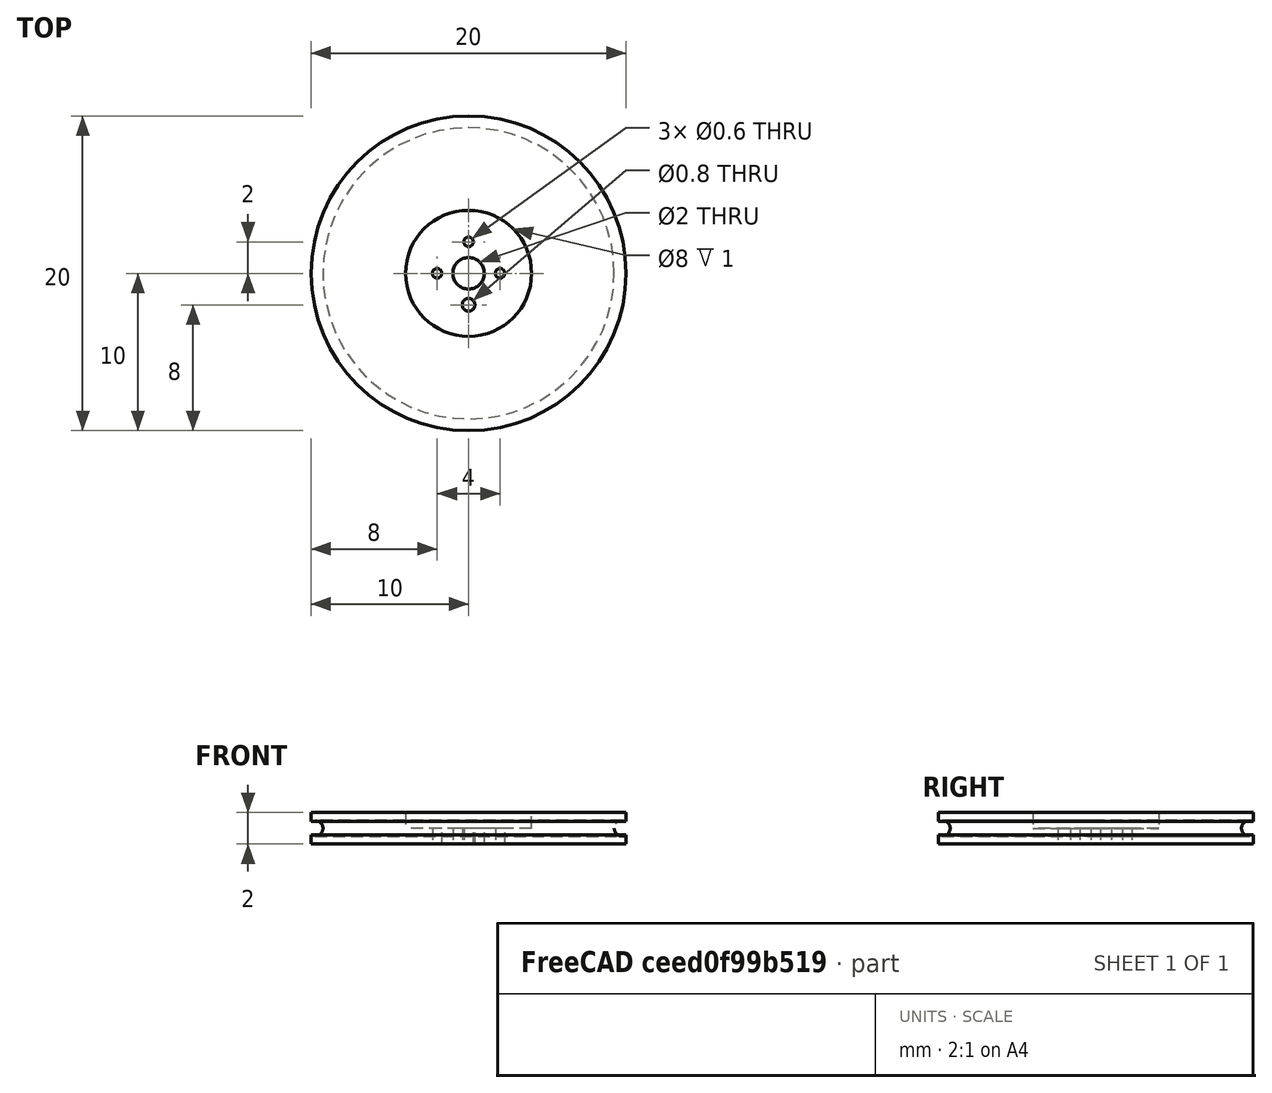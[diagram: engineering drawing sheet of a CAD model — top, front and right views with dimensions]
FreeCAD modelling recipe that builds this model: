
FCSTD DOCUMENT  (FreeCAD 0.20R29410 (Git))
Label: rueda
License: Creative Commons Attribution
LicenseURL: http://creativecommons.org/licenses/by/4.0/
objects: Part::Cylinder×7, Part::Cut×7, Part::Torus×1
note: 15 computed .brp shape members not serialized (recipe doc carries the construction recipe); baked Part::Feature solids carry a one-line shape summary decoded from their .brp

FEATURE [Part::Cylinder] Cylinder  label="Cilindro"
  Angle = 360
  AttacherType = Attacher::AttachEngine3D
  FirstAngle = 0
  Height = 2
  Radius = 10
  SecondAngle = 0
FEATURE [Part::Torus] Torus  label="Toro"
  Angle1 = -180
  Angle2 = 180
  Angle3 = 360
  AttacherType = Attacher::AttachEngine3D
  Placement = pos=(0,0,1) rot=(0,0,1;0rad)
  Radius1 = 9.75
  Radius2 = 0.5
FEATURE [Part::Cut] Cut
  Base = -> Cylinder
  Refine = true
  Tool = -> Torus
FEATURE [Part::Cylinder] Cylinder001  label="Cilindro001"
  Angle = 360
  AttacherType = Attacher::AttachEngine3D
  FirstAngle = 0
  Height = 1
  Placement = pos=(0,0,1) rot=(0,0,1;0rad)
  Radius = 4
  SecondAngle = 0
FEATURE [Part::Cut] Cut001  label="rueda con hueco"
  Base = -> Cut
  Refine = true
  Tool = -> Cylinder001
FEATURE [Part::Cylinder] Cylinder002  label="Cilindro002"
  Angle = 360
  AttacherType = Attacher::AttachEngine3D
  FirstAngle = 0
  Height = 10
  Radius = 1
  SecondAngle = 0
FEATURE [Part::Cut] Cut002
  Base = -> Cut001
  Refine = true
  Tool = -> Cylinder002
FEATURE [Part::Cylinder] Cylinder003  label="Cilindro003"
  Angle = 360
  AttacherType = Attacher::AttachEngine3D
  FirstAngle = 0
  Height = 10
  Placement = pos=(-2,0,0) rot=(0,0,1;0rad)
  Radius = 0.3
  SecondAngle = 0
FEATURE [Part::Cut] Cut003
  Base = -> Cut002
  Refine = true
  Tool = -> Cylinder003
FEATURE [Part::Cylinder] Cylinder004  label="Cilindro004"
  Angle = 360
  AttacherType = Attacher::AttachEngine3D
  FirstAngle = 0
  Height = 10
  Placement = pos=(2,0,0) rot=(0,0,1;0rad)
  Radius = 0.3
  SecondAngle = 0
FEATURE [Part::Cut] Cut004
  Base = -> Cut003
  Refine = true
  Tool = -> Cylinder004
FEATURE [Part::Cylinder] Cylinder005  label="Cilindro005"
  Angle = 360
  AttacherType = Attacher::AttachEngine3D
  FirstAngle = 0
  Height = 10
  Placement = pos=(0,2,0) rot=(0,0,1;0rad)
  Radius = 0.3
  SecondAngle = 0
FEATURE [Part::Cut] Cut005
  Base = -> Cut004
  Refine = true
  Tool = -> Cylinder005
FEATURE [Part::Cylinder] Cylinder006  label="Cilindro006"
  Angle = 360
  AttacherType = Attacher::AttachEngine3D
  FirstAngle = 0
  Height = 10
  Placement = pos=(0,-2,0) rot=(0,0,1;0rad)
  Radius = 0.4
  SecondAngle = 0
FEATURE [Part::Cut] Cut006  label="Rueda"
  Base = -> Cut005
  Refine = true
  Tool = -> Cylinder006
